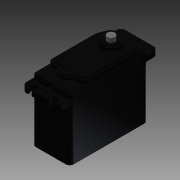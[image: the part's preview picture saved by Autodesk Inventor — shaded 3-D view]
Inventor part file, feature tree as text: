
AUTODESK INVENTOR PART (.ipt)
format: ipt  version: 2014 (Build 180170000, 170)  size: 344,576 bytes
history: native  units: in
note: dims shown in document units (in); Inventor stores cm internally (conversion verified against a paired STEP export)
features: extrude x15, sketch x15, fillet x2, projected_geometry x2, plane x1
ambient origin geometry x8: Origin, YZ Plane, XZ Plane, XY Plane, X Axis, Y Axis, Z Axis, Center Point
bodies: Solid1 (feature_tree)
feature tree (35):
  extrude  "Extrusion1"  Depth=1.832in
  extrude  "Extrusion2"  Depth=1.04in
  extrude  "Extrusion3"  Depth=0.04in TaperAngle=0.0deg
  extrude  "Extrusion4"  Depth=0.449in
  extrude  "Extrusion5"  Depth=0.0835in
  fillet  "Fillet1"  Radius=0.0835in
  plane  "Work Plane1"
  extrude  "Extrusion6"  Depth=0.9645in
  fillet  "Fillet2"  Radius=0.0175in
  extrude  "Extrusion7"  [1 undecoded]
  extrude  "Extrusion8"  Depth=2.907in
  extrude  "Extrusion9"  Depth=0.125in
  extrude  "Extrusion10"  Depth=0.149in
  extrude  "Extrusion11"  Depth=0.17in
  extrude  "Extrusion12"  Depth=0.1575in TaperAngle=0.0deg
  extrude  "Extrusion13"  Depth=0.1035in
  extrude  "Extrusion14"  Depth=0.08in
  extrude  "Extrusion15"  Depth=0.0645in TaperAngle=0.0deg
  sketch  "Sketch1"  dims[d0=2.309in d1=1.832in]
  sketch  "Sketch2"  dims[d2=1.121in d3=0.0in d4=1.04in]
  sketch  "Sketch3"  dims[d5=2.2635in d7=0.04in d8=0.0in]
  projected_geometry  "Projected Loop1"
  sketch  "Sketch4"  dims[d9=0.026in d10=0.449in]
  sketch  "Sketch5"  dims[d12=0.488in d13=0.189in d14=0.0835in d15=0.0in]
  sketch  "Sketch6"  dims[d16=0.044in d17=0.0in d18=0.9645in d19=0.0175in d20=0.0in]
  projected_geometry  "Projected Loop2"
  sketch  "Sketch7"  dims[d21=0.125in d22=-0.103in]
  sketch  "Sketch8"  dims[d23=1.0915in d24=2.907in]
  sketch  "Sketch9"  dims[d25=0.1575in d26=0.0in d27=0.125in]
  sketch  "Sketch10"  dims[d28=0.149in d29=0.149in]
  sketch  "Sketch11"  dims[d30=0.1995in d31=0.17in]
  sketch  "Sketch12"  dims[d32=0.17in d33=0.1575in d34=0.0in]
  sketch  "Sketch13"  dims[d35=0.184in d36=0.1035in]
  sketch  "Sketch14"  dims[d37=0.1575in d38=0.0in d39=0.08in]
  sketch  "Sketch15"  dims[d40=0.1345in d41=0.0645in d42=0.0in d43=0.5455in d44=0.077in d45=0.0in d46=0.43in d47=0.025in d48=0.0in d49=0.225in d50=0.127in d51=0.0in d52=0.1405in d53=0.1465in d54=0.293in d55=0.137in d56=0.241in d57=-0.0687in d58=1.0in d59=0.0in d60=1.0in d61=0.0in]
note: 1 required parameter value undecoded (feature->parameter linkage not recoverable at this tier; creation-order binding heuristic only, values carry confidence <= 0.55)
